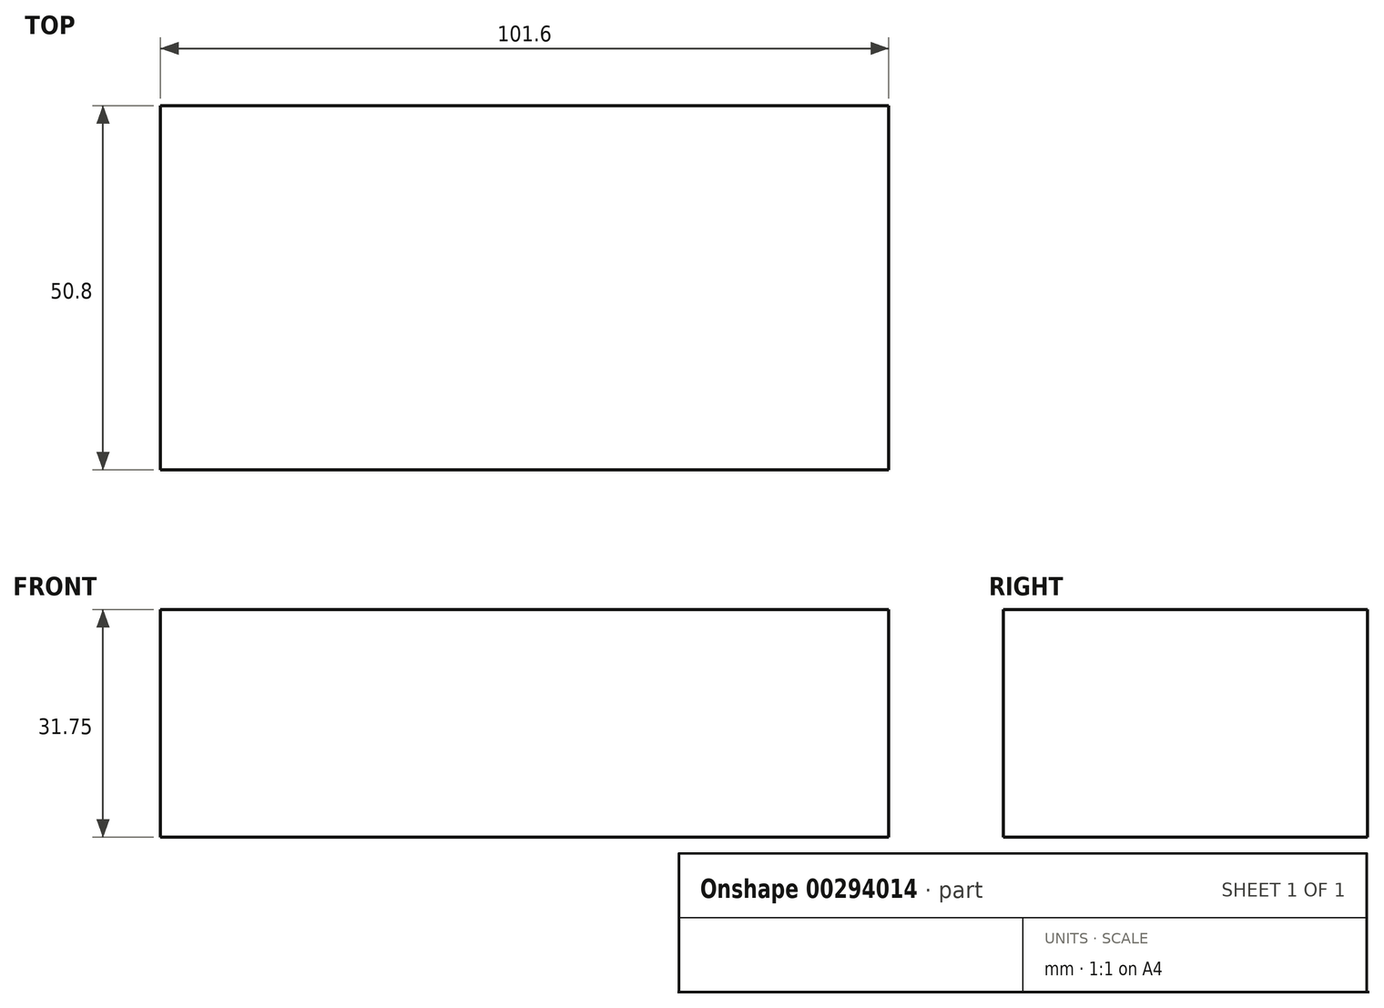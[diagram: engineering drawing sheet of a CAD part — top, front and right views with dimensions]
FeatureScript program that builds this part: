
annotation { "Feature Type Name" : "Feature", "Feature Type Description" : "" }
export const myFeature = defineFeature(function(context is Context, id is Id, definition is map)
    precondition{}
    {
        {
            var Q0;
            Q0=qCreatedBy(makeId("Top.planeOp"),FACE);
            var sketch = newSketch(context, id + "F0", { "sketchPlane" : qUnion([Q0])});
            skLineSegment(sketch, "E0.bottom", {"start": v(50.8, 25.4) * mm, "end": v(-50.8, 25.4) * mm});
            skLineSegment(sketch, "E0.top", {"start": v(50.8, -25.4) * mm, "end": v(-50.8, -25.4) * mm});
            skLineSegment(sketch, "E0.left", {"start": v(50.8, 25.4) * mm, "end": v(50.8, -25.4) * mm});
            skLineSegment(sketch, "E0.right", {"start": v(-50.8, 25.4) * mm, "end": v(-50.8, -25.4) * mm});
            skPoint(sketch, "E0.middle", {"position": v(0, 0) * mm});
            skSolve(sketch);
        }
        {
            var Q0;
            Q0 = qSketchRegion(id + "F0", true);
            extrude(context, id + "F1", {"entities" : qUnion([Q0]), "depth" : 31.75 * mm});
        }
    });
